# Revit family: Type A Configuration Basin and Shelf
name_source: partatom
category: Plumbing Fixtures
revit_build: Autodesk Revit 2016 (Build: 20160314_0715(x64)
units: mm (PartAtom-declared; Revit-internal decimal feet)

## family parameters
Always vertical = Yes
Cut with Voids When Loaded = No
OmniClass Number = 23.45.00.00
OmniClass Title = Sanitary, Laundry, and Cleaning Equipment
Part Type = Normal
Room Calculation Point = No
Round Connector Dimension = Use Diameter
Shared = No
Work Plane-Based = No

## types (1)
- Type A Configuration Basin and Shelf
    Basin&Mirror_Horizontal_Offset = 425 mm  [stored 1.39436 ft]
    Basin&Mirror_Horizontal_calc = 425 mm  [stored 1.39436 ft]
    CirculationSpace = Yes
    HandBasin_Vertical_Offset = 830 mm  [stored 2.7231 ft]
    HandBasin_Vertical_calc = 830 mm  [stored 2.7231 ft]
    Mirror = Yes
    Mirror_Vertical_Offset = 900 mm  [stored 2.95276 ft]
    Mirror_Vertical_calc = 900 mm  [stored 2.95276 ft]
    Tap Hot/Cold = No
    Tap Warm/Cold = Yes

note: [stored X ft] marks values corroborated as IEEE doubles in the binary element streams (Revit-internal decimal feet)

## geometry (parser evidence)
native form markers: Blend x10, Sweep x5
no freeform markers — native parametric forms only
